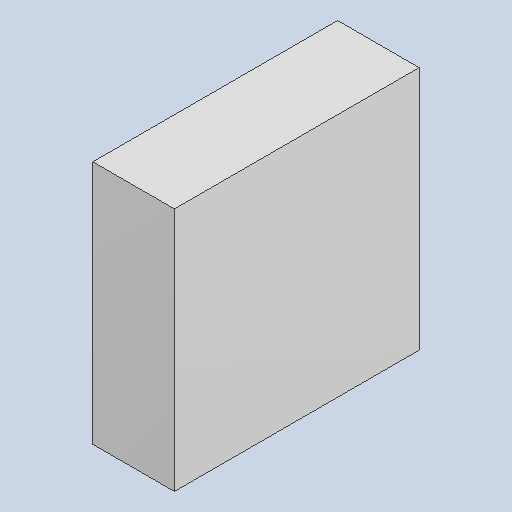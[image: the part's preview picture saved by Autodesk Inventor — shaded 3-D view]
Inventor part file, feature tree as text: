
AUTODESK INVENTOR PART (.ipt)
format: ipt  version: 2023.4 (Build 274418000, 418)  size: 81,408 bytes
history: native  units: mm
features: extrude x1
ambient origin geometry x8: Origin, YZ Plane, XZ Plane, XY Plane, X Axis, Y Axis, Z Axis, Center Point
bodies: Solid1 (feature_tree)
feature tree (1):
  extrude  "Extruded_30"  [1 undecoded]
note: 1 required parameter value undecoded (feature->parameter linkage not recoverable at this tier; creation-order binding heuristic only, values carry confidence <= 0.55)
